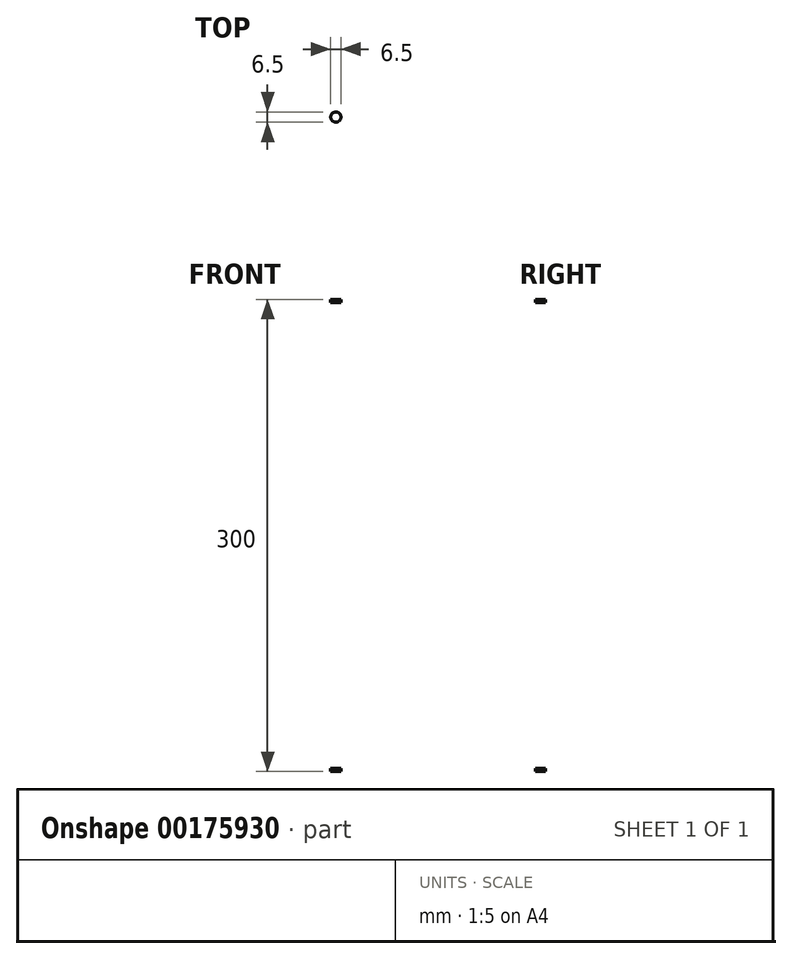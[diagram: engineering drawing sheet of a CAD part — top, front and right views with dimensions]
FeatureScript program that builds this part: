
annotation { "Feature Type Name" : "Feature", "Feature Type Description" : "" }
export const myFeature = defineFeature(function(context is Context, id is Id, definition is map)
    precondition{}
    {
        {
            var Q0;
            Q0=qCreatedBy(makeId("Front.planeOp"),FACE);
            var sketch = newSketch(context, id + "F0", { "sketchPlane" : qUnion([Q0])});
            skLineSegment(sketch, "E0", {"start": v(20, 150) * mm, "end": v(0, 150) * mm});
            skLineSegment(sketch, "E1", {"start": v(0, 150) * mm, "end": v(0, 0) * mm});
            skLineSegment(sketch, "E2.0", {"start": v(2, 148) * mm, "end": v(2, 0) * mm});
            skLineSegment(sketch, "E2.1", {"start": v(20, 148) * mm, "end": v(2, 148) * mm});
            skLineSegment(sketch, "E3", {"start": v(20, 148) * mm, "end": v(20, 150) * mm});
            skLineSegment(sketch, "E4.MirrorCS", {"start": v(20, -148) * mm, "end": v(20, -150) * mm});
            skLineSegment(sketch, "E5.MirrorCS", {"start": v(20, -150) * mm, "end": v(0, -150) * mm});
            skLineSegment(sketch, "E6.MirrorCS", {"start": v(20, -148) * mm, "end": v(2, -148) * mm});
            skLineSegment(sketch, "E7.MirrorCS", {"start": v(2, -148) * mm, "end": v(2, 0) * mm});
            skLineSegment(sketch, "E8.MirrorCS", {"start": v(0, -150) * mm, "end": v(0, 0) * mm});
            skSolve(sketch);
        }
        {
            var Q0;
            Q0=makeQuery(id+"F0.imprint","IMPRINT",FACE,{"disambiguationData":[TD([[makeQuery(id+"F0.imprint","IMPRINT",EDGE,{"derivedFrom":sQuery(id+"F0.wireOp",EDGE,"E0")}),1.0]])]});
            extrude(context, id + "F1", {"entities" : qUnion([Q0]), "endBound" : BoundingType.SYMMETRIC, "depth" : 365 * mm});
        }
        {
            var Q0;
            Q0=makeQuery(id+"F1.opExtrude","SWEPT_FACE",FACE,{"disambiguationData":[OSD([sQuery(id+"F0.wireOp",EDGE,"E5.MirrorCS")])]});
            var sketch = newSketch(context, id + "F2", { "sketchPlane" : qUnion([Q0])});
            skCircle(sketch, "E9", {"center": v(10, 132.5) * mm, "radius": 3.25 * mm});
            skCircle(sketch, "E10.MirrorC", {"center": v(10, -132.5) * mm, "radius": 3.25 * mm});
            skSolve(sketch);
        }
        {
            var Q0;
            Q0=makeQuery(id+"F2.imprint","IMPRINT",FACE,{"disambiguationData":[TD([[makeQuery(id+"F2.imprint","IMPRINT",EDGE,{"derivedFrom":sQuery(id+"F2.wireOp",EDGE,"E9")}),1.0]])]});
            var Q1;
            Q1=makeQuery(id+"F2.imprint","IMPRINT",FACE,{"disambiguationData":[TD([[makeQuery(id+"F2.imprint","IMPRINT",EDGE,{"derivedFrom":sQuery(id+"F2.wireOp",EDGE,"E10.MirrorC")}),-1.0]])]});
            extrude(context, id + "F3", {"entities" : qUnion([Q0, Q1]), "operationType" : NewBodyOperationType.REMOVE, "endBound" : BoundingType.THROUGH_ALL, "oppositeDirection" : true, "depth" : 25 * mm});
        }
    });
